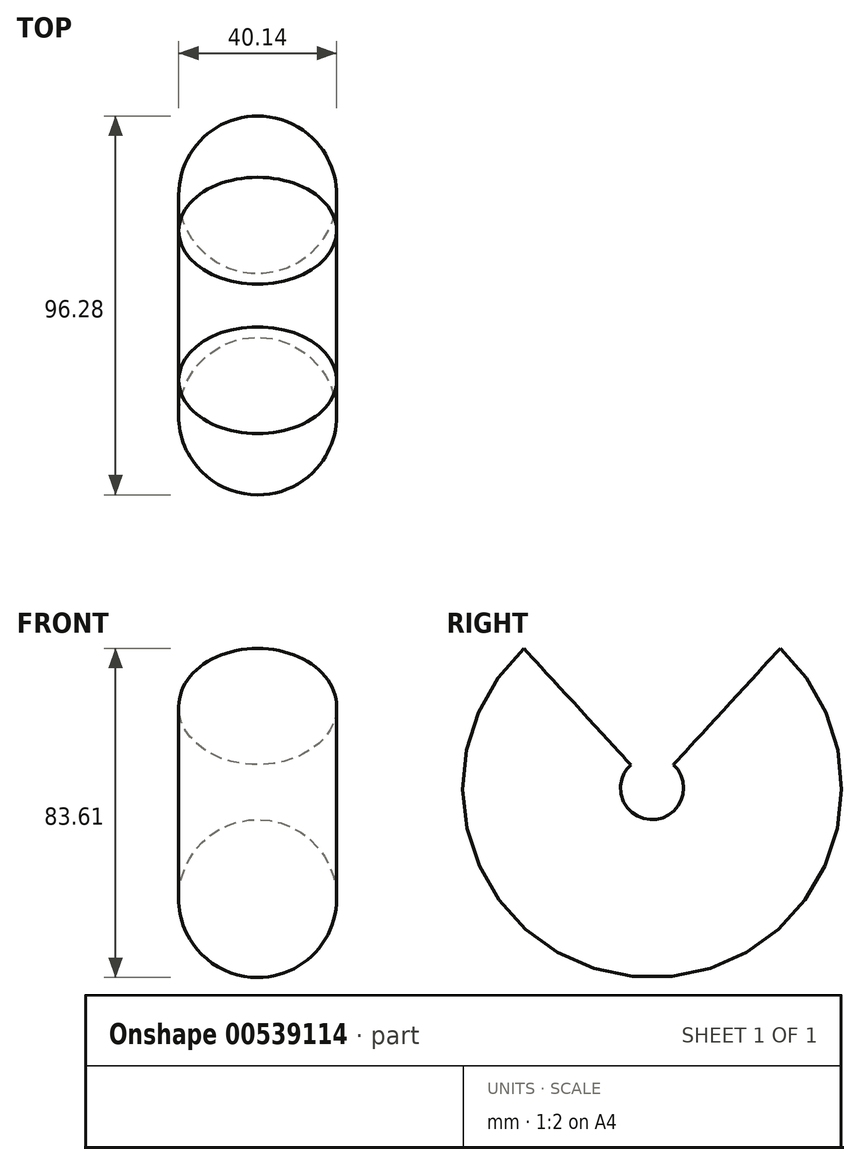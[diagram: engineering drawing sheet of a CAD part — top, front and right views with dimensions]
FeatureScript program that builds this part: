
annotation { "Feature Type Name" : "Feature", "Feature Type Description" : "" }
export const myFeature = defineFeature(function(context is Context, id is Id, definition is map)
    precondition{}
    {
        {
            var Q0;
            Q0=qCreatedBy(makeId("Front.planeOp"),FACE);
            var sketch = newSketch(context, id + "F0", { "sketchPlane" : qUnion([Q0])});
            skLineSegment(sketch, "E0.bottom", {"start": v(-112.8, 50.7) * mm, "end": v(-58.2, 50.7) * mm});
            skLineSegment(sketch, "E0.top", {"start": v(-112.8, -31.65) * mm, "end": v(-58.2, -31.65) * mm});
            skLineSegment(sketch, "E0.left", {"start": v(-112.8, 50.7) * mm, "end": v(-112.8, -31.65) * mm});
            skLineSegment(sketch, "E0.right", {"start": v(-58.2, 50.7) * mm, "end": v(-58.2, -31.65) * mm});
            skCircle(sketch, "E1", {"center": v(61.2, 22.61) * mm, "radius": 20.07 * mm});
            skSolve(sketch);
        }
        {
            var Q0;
            Q0=makeQuery(id+"F0.imprint","IMPRINT",FACE,{"disambiguationData":[TD([[makeQuery(id+"F0.imprint","IMPRINT",EDGE,{"derivedFrom":sQuery(id+"F0.wireOp",EDGE,"E1")}),1.0]])]});
            var Q1;
            Q1=sQuery(id+"F0.wireOp",EDGE,"E0.bottom");
            revolve(context, id + "F1", {"entities" : qUnion([Q0]), "axis" : qUnion([Q1]), "revolveType" : RevolveType.SYMMETRIC, "angle" : 274.91 * degree});
        }
    });
